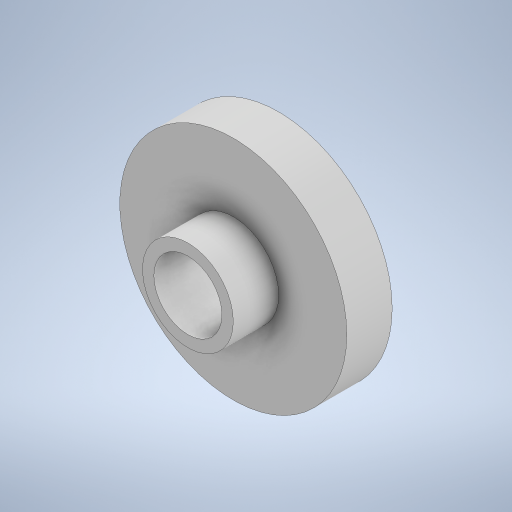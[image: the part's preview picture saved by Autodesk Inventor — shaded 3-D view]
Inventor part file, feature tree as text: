
AUTODESK INVENTOR PART (.ipt)
format: ipt  version: 2024 (Build 280153000, 153)  size: 256,512 bytes
history: native  units: in
note: dims shown in document units (in); Inventor stores cm internally (conversion verified against a paired STEP export)
features: extrude x3, sketch x2, mirror x1
ambient origin geometry x8: Origin, YZ Plane, XZ Plane, XY Plane, X Axis, Y Axis, Z Axis, Center Point
bodies: Solid1 (feature_tree)
feature tree (6):
  extrude  "Extrusion1"  Depth=0.0394in TaperAngle=0.0deg
  sketch  "Sketch2"  dims[d3=0.1181in d4=0.1575in d5=0.0591in d6=0.0in d7=0.0787in d8=0.0in]
  extrude  "Extrusion2"  Depth=0.1575in
  extrude  "Extrusion3"  Depth=0.0591in TaperAngle=0.0deg
  mirror  "Mirror2"
  sketch  "Sketch1"  dims[d0=0.3937in d1=0.0394in d2=0.0in]
